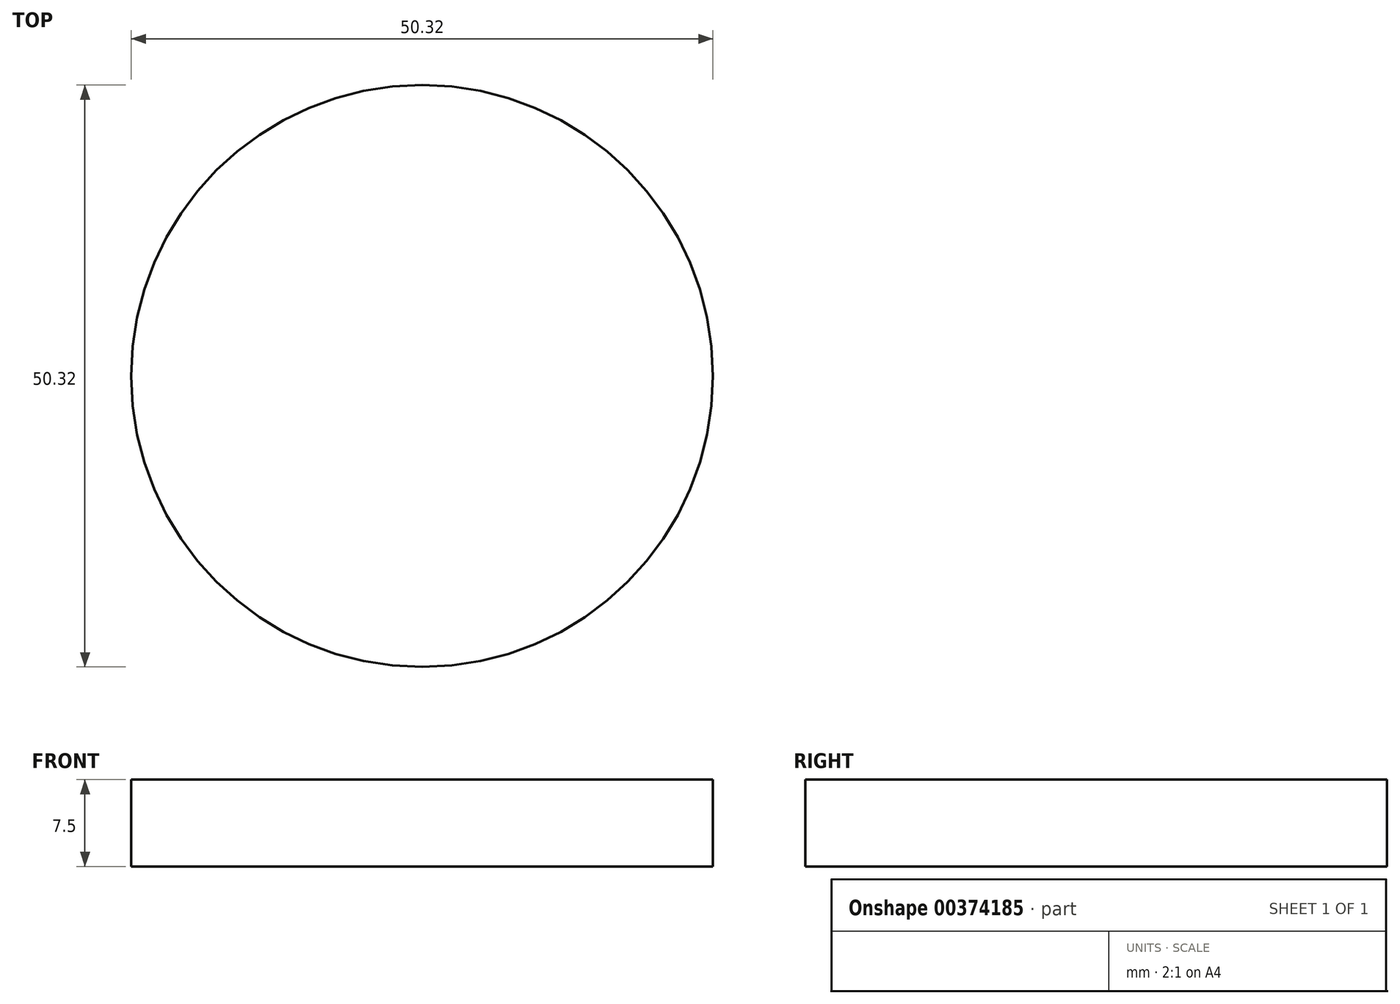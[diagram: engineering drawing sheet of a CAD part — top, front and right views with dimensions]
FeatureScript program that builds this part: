
annotation { "Feature Type Name" : "Feature", "Feature Type Description" : "" }
export const myFeature = defineFeature(function(context is Context, id is Id, definition is map)
    precondition{}
    {
        {
            var Q0;
            Q0=qCreatedBy(makeId("Top.planeOp"),FACE);
            var sketch = newSketch(context, id + "F0", { "sketchPlane" : qUnion([Q0])});
            skCircle(sketch, "E0", {"center": v(0, 0) * mm, "radius": 25.16 * mm});
            skSolve(sketch);
        }
        {
            var Q0;
            Q0 = qSketchRegion(id + "F0", true);
            extrude(context, id + "F1", {"entities" : qUnion([Q0]), "depth" : 7.5 * mm});
        }
    });
